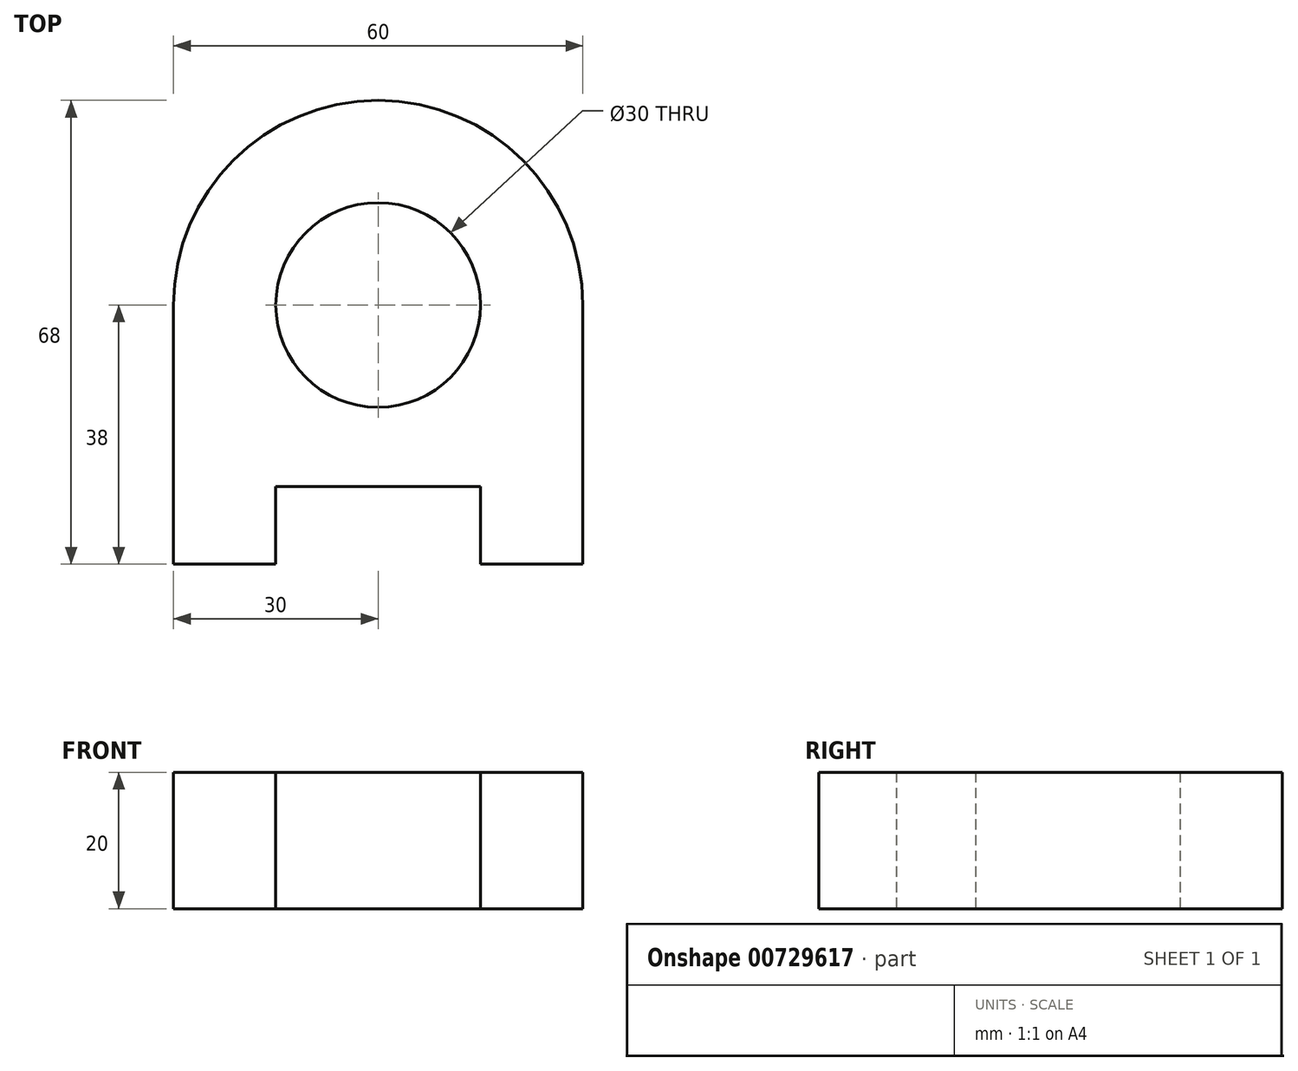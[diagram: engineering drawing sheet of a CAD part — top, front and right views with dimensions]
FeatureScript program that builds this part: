
annotation { "Feature Type Name" : "Feature", "Feature Type Description" : "" }
export const myFeature = defineFeature(function(context is Context, id is Id, definition is map)
    precondition{}
    {
        {
            var Q0;
            Q0=qCreatedBy(makeId("Top.planeOp"),FACE);
            var sketch = newSketch(context, id + "F0", { "sketchPlane" : qUnion([Q0])});
            skLineSegment(sketch, "E0", {"start": v(0, 0) * mm, "end": v(0, 38) * mm});
            skLineSegment(sketch, "E1", {"start": v(60, 38) * mm, "end": v(60, 0) * mm});
            skLineSegment(sketch, "E2", {"start": v(60, 0) * mm, "end": v(45, 0) * mm});
            skLineSegment(sketch, "E3", {"start": v(45, 0) * mm, "end": v(45, 11.36) * mm});
            skLineSegment(sketch, "E4", {"start": v(45, 11.36) * mm, "end": v(15, 11.36) * mm});
            skLineSegment(sketch, "E5", {"start": v(15, 11.36) * mm, "end": v(15, 0) * mm});
            skLineSegment(sketch, "E6", {"start": v(15, 0) * mm, "end": v(0, 0) * mm});
            skArc(sketch, "E7", {"start": v(60, 38) * mm, "mid": v(30, 68) * mm, "end": v(0, 38) * mm});
            skCircle(sketch, "E8", {"center": v(30, 38) * mm, "radius": 15 * mm});
            skSolve(sketch);
        }
        {
            var Q0;
            Q0 = qSketchRegion(id + "F0", true);
            extrude(context, id + "F1", {"entities" : qUnion([Q0]), "depth" : 20 * mm, "offsetDistance" : 25 * mm});
        }
    });
